# Revit family: Lighting-Linear-Acclaim-Linear One DMX Exterior
name_source: partatom
category: Lighting Fixtures
revit_build: Autodesk Revit 2017 (Build: 20190508_0315(x64)
units: mm (PartAtom-declared; Revit-internal decimal feet)

## family parameters
Cut with Voids When Loaded = No
Host = Face
Light Source = Yes
Part Type = Normal
Room Calculation Point = No
Round Connector Dimension = Use Diameter
Shared = No

## types (6) — shared parameters
Apparent Load = 0 VA
Color Filter = 16777215
Default Elevation = 48 "
Description = Linear LED
Dimming Lamp Color Temperature Shift = <None>
Emit from Line Length = 48 "
Housing Finish = Aluminum
Lamp = LED
Length = 48 "
Manufacturer = Acclaim Lighting
Model = Linear One
Number of Poles = 1
Photometric Web File = Load File
Power Factor = 1
Tilt Angle = -90.00°
URL = http://www.acclaimlighting.com
Voltage = 0 V
Width = 2.13 "

## per-type parameters (varying)
| type | Height |
| Standard Glare Shield | 3.78 " |
| Standard Louver | 4.51 " |
| Flat Mount Glare Shield | 3.94 " |
| Flat Mount Louver | 3.94 " |
| Flat Mount | 3.19 " |
| Standard | 3.78 " |

## geometry (parser evidence)
native form markers: Blend x13, Sweep x2
no freeform markers — native parametric forms only
